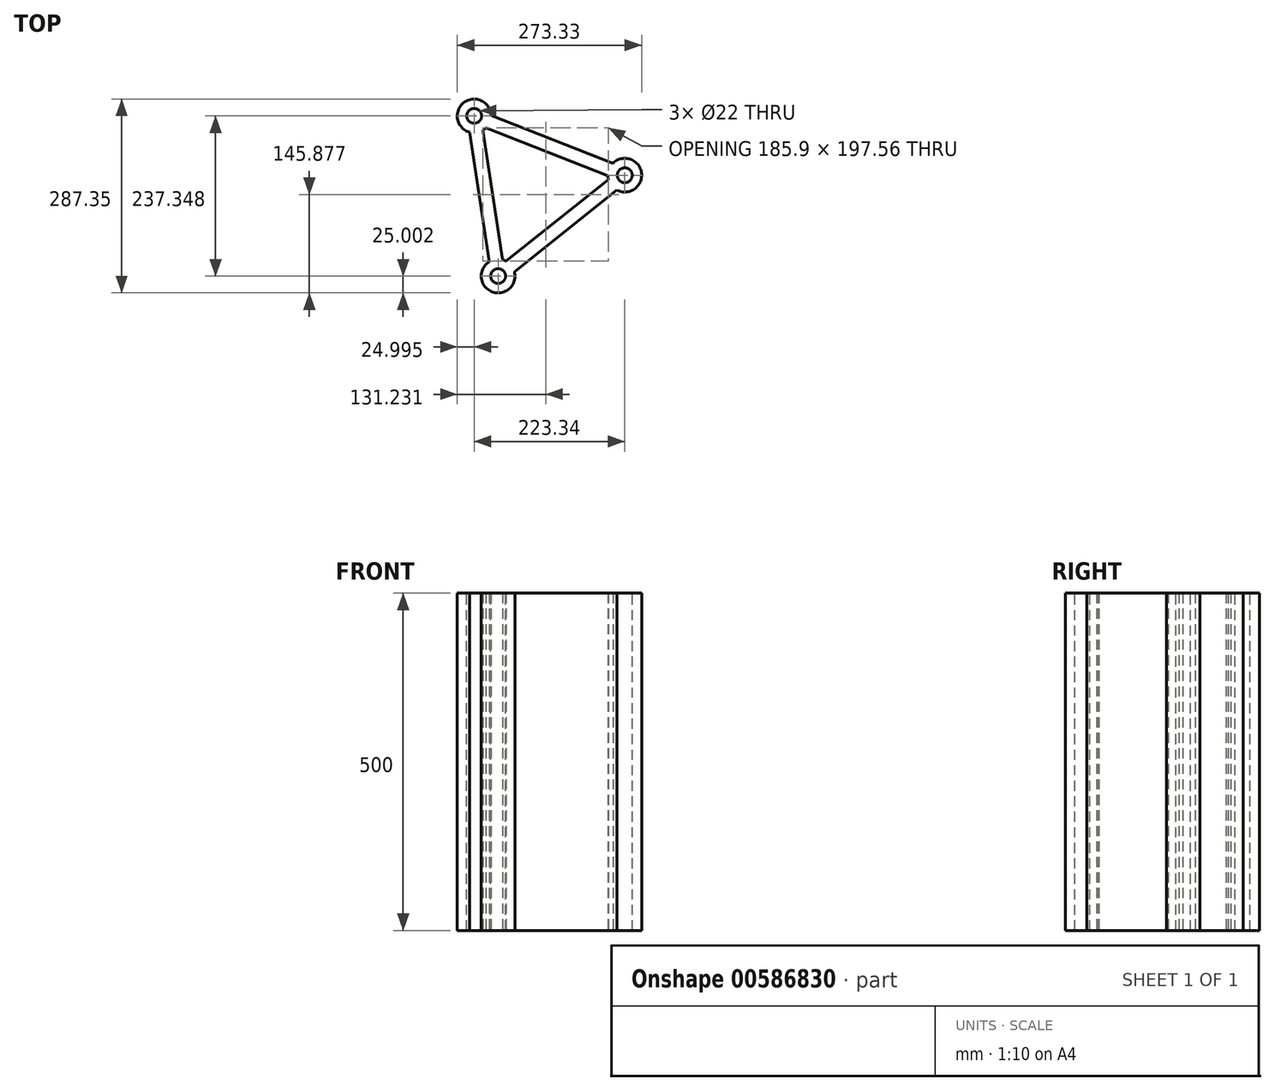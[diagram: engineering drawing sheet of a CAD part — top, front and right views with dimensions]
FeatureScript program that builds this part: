
annotation { "Feature Type Name" : "Feature", "Feature Type Description" : "" }
export const myFeature = defineFeature(function(context is Context, id is Id, definition is map)
    precondition{}
    {
        {
            assignVariable(context, id + "F0", {"name" : "Length", "anyValue" : 500});
        }
        {
            var Q0;
            Q0=qCreatedBy(makeId("Top.planeOp"),FACE);
            var sketch = newSketch(context, id + "F1", { "sketchPlane" : qUnion([Q0])});
            skCircle(sketch, "E0", {"center": v(-180.71, 87.86) * mm, "radius": 25 * mm});
            skCircle(sketch, "E1", {"center": v(42.62, 0) * mm, "radius": 25 * mm});
            skCircle(sketch, "E2", {"center": v(-145.13, -149.49) * mm, "radius": 25 * mm});
            skLineSegment(sketch, "E3", {"start": v(-180.71, 87.86) * mm, "end": v(42.62, 0) * mm, "construction": true});
            skLineSegment(sketch, "E4", {"start": v(42.62, 0) * mm, "end": v(-145.13, -149.49) * mm, "construction": true});
            skLineSegment(sketch, "E5", {"start": v(-180.71, 87.86) * mm, "end": v(-145.13, -149.49) * mm, "construction": true});
            skLineSegment(sketch, "E6", {"start": v(-155.73, 88.78) * mm, "end": v(24.96, 17.7) * mm});
            skLineSegment(sketch, "E7", {"start": v(-163.05, 70.17) * mm, "end": v(17.64, -0.92) * mm});
            skLineSegment(sketch, "E8", {"start": v(-133.44, -127.4) * mm, "end": v(18.47, -6.45) * mm});
            skLineSegment(sketch, "E9", {"start": v(-120.98, -143.04) * mm, "end": v(30.93, -22.1) * mm});
            skLineSegment(sketch, "E10", {"start": v(-167.43, 66.68) * mm, "end": v(-138.64, -125.35) * mm});
            skLineSegment(sketch, "E11", {"start": v(-187.2, 63.72) * mm, "end": v(-158.42, -128.31) * mm});
            skSolve(sketch);
        }
        {
            var Q0;
            {var subQ0=sQuery(id+"F1.wireOp",EDGE,"E0");var subQ1=makeQuery(id+"F1.imprint","INTERSECT",VERTEX,{"derivedFrom":[subQ0,sQuery(id+"F1.wireOp",EDGE,"E6")]});Q0=makeQuery(id+"F1.imprint","IMPRINT",FACE,{"disambiguationData":[TD([[makeQuery(id+"F1.imprint","IMPRINT",EDGE,{"disambiguationData":[TD([[subQ1,-1.0]])],"derivedFrom":subQ0}),1.0]])]});}
            var Q1;
            {var subQ0=sQuery(id+"F1.wireOp",EDGE,"E10");Q1=makeQuery(id+"F1.imprint","IMPRINT",FACE,{"disambiguationData":[TD([[makeQuery(id+"F1.imprint","IMPRINT",EDGE,{"derivedFrom":subQ0}),-1.0]])]});}
            var Q2;
            {var subQ0=sQuery(id+"F1.wireOp",EDGE,"E2");var subQ1=makeQuery(id+"F1.imprint","INTERSECT",VERTEX,{"derivedFrom":[subQ0,sQuery(id+"F1.wireOp",EDGE,"E8")]});Q2=makeQuery(id+"F1.imprint","IMPRINT",FACE,{"disambiguationData":[TD([[makeQuery(id+"F1.imprint","IMPRINT",EDGE,{"disambiguationData":[TD([[subQ1,1.0]])],"derivedFrom":subQ0}),1.0]])]});}
            var Q3;
            {var subQ0=sQuery(id+"F1.wireOp",EDGE,"E8");Q3=makeQuery(id+"F1.imprint","IMPRINT",FACE,{"disambiguationData":[TD([[makeQuery(id+"F1.imprint","IMPRINT",EDGE,{"derivedFrom":subQ0}),-1.0]])]});}
            var Q4;
            {var subQ0=sQuery(id+"F1.wireOp",EDGE,"E1");var subQ1=makeQuery(id+"F1.imprint","INTERSECT",VERTEX,{"derivedFrom":[subQ0,sQuery(id+"F1.wireOp",EDGE,"E6")]});Q4=makeQuery(id+"F1.imprint","IMPRINT",FACE,{"disambiguationData":[TD([[makeQuery(id+"F1.imprint","IMPRINT",EDGE,{"disambiguationData":[TD([[subQ1,-1.0]])],"derivedFrom":subQ0}),1.0]])]});}
            var Q5;
            {var subQ0=sQuery(id+"F1.wireOp",EDGE,"E6");Q5=makeQuery(id+"F1.imprint","IMPRINT",FACE,{"disambiguationData":[TD([[makeQuery(id+"F1.imprint","IMPRINT",EDGE,{"derivedFrom":subQ0}),-1.0]])]});}
            extrude(context, id + "F2", {"entities" : qUnion([Q0, Q1, Q2, Q3, Q4, Q5]), "depth" : (getVariable(context, 'Length')) * mm, "offsetDistance" : 25 * mm});
        }
        {
            var Q0;
            Q0=makeQuery(id+"F2.opExtrude","CAP_FACE",FACE,{"disambiguationData":[OSD([sQuery(id+"F1.wireOp",EDGE,"E0"),sQuery(id+"F1.wireOp",EDGE,"E1"),sQuery(id+"F1.wireOp",EDGE,"E2"),sQuery(id+"F1.wireOp",EDGE,"E6"),sQuery(id+"F1.wireOp",EDGE,"E7"),sQuery(id+"F1.wireOp",EDGE,"E8"),sQuery(id+"F1.wireOp",EDGE,"E9"),sQuery(id+"F1.wireOp",EDGE,"E10"),sQuery(id+"F1.wireOp",EDGE,"E11")])],"isStart":false});
            var sketch = newSketch(context, id + "F3", { "sketchPlane" : qUnion([Q0])});
            skPoint(sketch, "E12", {"position": v(-180.71, 87.86) * mm});
            skPoint(sketch, "E13", {"position": v(42.62, 0) * mm});
            skPoint(sketch, "E14", {"position": v(-145.13, -149.49) * mm});
            skSolve(sketch);
        }
        {
            var Q0;
            Q0=sQuery(id+"F3.wireOp",VERTEX,"E12");
            var Q1;
            Q1=sQuery(id+"F3.wireOp",VERTEX,"E13");
            var Q2;
            Q2=sQuery(id+"F3.wireOp",VERTEX,"E14");
            var Q3;
            Q3=makeQuery(id+"F2.opExtrude","SWEPT_BODY",BODY,{"disambiguationData":[OSD([sQuery(id+"F1.wireOp",EDGE,"E0"),sQuery(id+"F1.wireOp",EDGE,"E1"),sQuery(id+"F1.wireOp",EDGE,"E2"),sQuery(id+"F1.wireOp",EDGE,"E6"),sQuery(id+"F1.wireOp",EDGE,"E7"),sQuery(id+"F1.wireOp",EDGE,"E8"),sQuery(id+"F1.wireOp",EDGE,"E9"),sQuery(id+"F1.wireOp",EDGE,"E10"),sQuery(id+"F1.wireOp",EDGE,"E11")])]});
            hole(context, id + "F4", {"style" : HoleStyle.SIMPLE, "endStyle" : HoleEndStyle.BLIND, "standardTappedOrClearance" : lookupTablePath({ "standard" : "ISO", "fit" : "Normal", "size" : "M20", "type" : "Clearance" }), "standardBlindInLast" : lookupTablePath({ "fit" : "Standard", "standard" : "ISO", "size" : "M20", "type" : "Clearance" }), "holeDiameter" : 22 * mm, "majorDiameter" : 20 * mm, "holeDepth" : (getVariable(context, 'Length')) * mm, "isTappedThrough" : true, "tappedDepth" : 12 * mm, "tapClearance" : 12, "locations" : qUnion([Q0, Q1, Q2]), "scope" : qUnion([Q3])});
        }
    });
